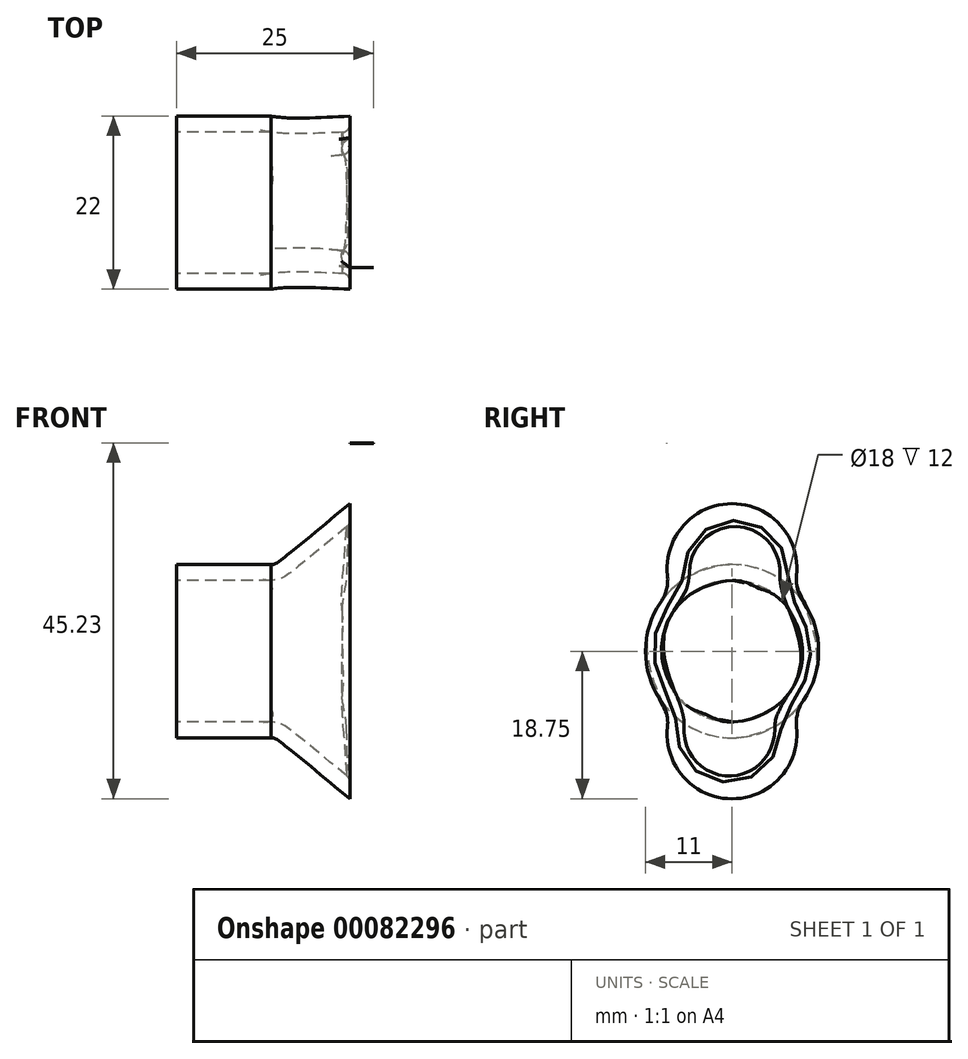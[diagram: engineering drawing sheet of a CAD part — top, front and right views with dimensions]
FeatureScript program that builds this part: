
annotation { "Feature Type Name" : "Feature", "Feature Type Description" : "" }
export const myFeature = defineFeature(function(context is Context, id is Id, definition is map)
    precondition{}
    {
        {
            var Q0;
            Q0=qCreatedBy(makeId("Right.planeOp"),FACE);
            cPlane(context, id + "F0", {"entities" : qUnion([Q0]), "cplaneType" : CPlaneType.OFFSET, "offset" : 10 * mm, "oppositeDirection" : true, "width" : 150 * mm, "height" : 150 * mm});
        }
        {
            var Q0;
            Q0=qCreatedBy(makeId("Right.planeOp"),FACE);
            var sketch = newSketch(context, id + "F1", { "sketchPlane" : qUnion([Q0])});
            skArc(sketch, "E0", {"start": v(-8.2, -9.62) * mm, "mid": v(0, -18.75) * mm, "end": v(8.2, -9.62) * mm});
            skArc(sketch, "E1", {"start": v(8.2, 9.62) * mm, "mid": v(0, 18.75) * mm, "end": v(-8.2, 9.62) * mm});
            skArc(sketch, "E2", {"start": v(9.06, -6.24) * mm, "mid": v(11, 0) * mm, "end": v(9.06, 6.24) * mm});
            skPoint(sketch, "E3.visualSharp", {"position": v(-7.79, -7.77) * mm});
            skArc(sketch, "E3.filletArc", {"start": v(-8.2, -9.62) * mm, "mid": v(-8.33, -7.85) * mm, "end": v(-9.06, -6.24) * mm});
            skPoint(sketch, "E4.visualSharp", {"position": v(7.79, -7.77) * mm});
            skArc(sketch, "E4.filletArc", {"start": v(9.06, -6.24) * mm, "mid": v(8.33, -7.85) * mm, "end": v(8.2, -9.62) * mm});
            skArc(sketch, "E5.trimOffspring", {"start": v(-9.06, 6.24) * mm, "mid": v(-11, 0) * mm, "end": v(-9.06, -6.24) * mm});
            skPoint(sketch, "E6.visualSharp", {"position": v(-7.79, 7.77) * mm});
            skArc(sketch, "E6.filletArc", {"start": v(-9.06, 6.24) * mm, "mid": v(-8.33, 7.85) * mm, "end": v(-8.2, 9.62) * mm});
            skPoint(sketch, "E7.visualSharp", {"position": v(7.79, 7.77) * mm});
            skArc(sketch, "E7.filletArc", {"start": v(8.2, 9.62) * mm, "mid": v(8.33, 7.85) * mm, "end": v(9.06, 6.24) * mm});
            skSolve(sketch);
        }
        {
            var Q0;
            Q0=qCreatedBy(id+"F0.planeOp",FACE);
            var sketch = newSketch(context, id + "F2", { "sketchPlane" : qUnion([Q0])});
            skCircle(sketch, "E8", {"center": v(0, 0) * mm, "radius": 11 * mm});
            skSolve(sketch);
        }
        {
            var Q0;
            Q0=makeQuery(id+"F1.imprint","IMPRINT",FACE,{"disambiguationData":[TD([[makeQuery(id+"F1.imprint","IMPRINT",EDGE,{"derivedFrom":sQuery(id+"F1.wireOp",EDGE,"E0")}),1.0]])]});
            var Q1;
            Q1=makeQuery(id+"F2.imprint","IMPRINT",FACE,{"disambiguationData":[TD([[makeQuery(id+"F2.imprint","IMPRINT",EDGE,{"derivedFrom":sQuery(id+"F2.wireOp",EDGE,"E8")}),1.0]])]});
            loft(context, id + "F3", {"sheetProfilesArray" : [{ "sheetProfileEntities" : qUnion([Q0]) }, { "sheetProfileEntities" : qUnion([Q1]) }]});
        }
        {
            var Q0;
            Q0=makeQuery(id+"F3.opLoft","CAP_FACE",FACE,{"disambiguationData":[OSD([makeQuery(id+"F2.imprint","IMPRINT",FACE,{"disambiguationData":[TD([[makeQuery(id+"F2.imprint","IMPRINT",EDGE,{"derivedFrom":sQuery(id+"F2.wireOp",EDGE,"E8")}),1.0]])]})])],"isStart":true});
            var Q1;
            Q1=makeQuery(id+"F3.opLoft","CAP_FACE",FACE,{"disambiguationData":[OSD([makeQuery(id+"F1.imprint","IMPRINT",FACE,{"disambiguationData":[TD([[makeQuery(id+"F1.imprint","IMPRINT",EDGE,{"derivedFrom":sQuery(id+"F1.wireOp",EDGE,"E0")}),1.0]])]})])],"isStart":true});
            shell(context, id + "F4", {"entities" : qUnion([Q0, Q1]), "thickness" : 2 * mm});
        }
        {
            var Q0;
            Q0=makeQuery(id+"F2.imprint","IMPRINT",FACE,{"disambiguationData":[TD([[makeQuery(id+"F2.imprint","IMPRINT",EDGE,{"derivedFrom":sQuery(id+"F2.wireOp",EDGE,"E8")}),1.0]])]});
            extrude(context, id + "F5", {"entities" : qUnion([Q0]), "operationType" : NewBodyOperationType.ADD, "oppositeDirection" : true, "depth" : 12 * mm, "offsetDistance" : 25 * mm});
        }
        {
            var Q0;
            Q0=makeQuery(id+"F5.opExtrude","CAP_FACE",FACE,{"disambiguationData":[OSD([sQuery(id+"F2.wireOp",EDGE,"E8")])],"isStart":false});
            var sketch = newSketch(context, id + "F6", { "sketchPlane" : qUnion([Q0])});
            skPoint(sketch, "E9", {"position": v(0, 0) * mm});
            skSolve(sketch);
        }
        {
            var Q0;
            Q0=sQuery(id+"F6.wireOp",VERTEX,"E9");
            var Q1;
            Q1=makeQuery(id+"F3.opLoft","SWEPT_BODY",BODY,{"disambiguationData":[OSD([makeQuery(id+"F1.imprint","IMPRINT",FACE,{"disambiguationData":[TD([[makeQuery(id+"F1.imprint","IMPRINT",EDGE,{"derivedFrom":sQuery(id+"F1.wireOp",EDGE,"E0")}),1.0]])]}),makeQuery(id+"F2.imprint","IMPRINT",FACE,{"disambiguationData":[TD([[makeQuery(id+"F2.imprint","IMPRINT",EDGE,{"derivedFrom":sQuery(id+"F2.wireOp",EDGE,"E8")}),1.0]])]})])]});
            hole(context, id + "F7", {"style" : HoleStyle.SIMPLE, "endStyle" : HoleEndStyle.BLIND, "holeDiameter" : 18 * mm, "majorDiameter" : 5 * mm, "holeDepth" : 12 * mm, "isTappedThrough" : true, "tappedDepth" : 12 * mm, "tapClearance" : 3, "startFromSketch" : true, "locations" : qUnion([Q0]), "scope" : qUnion([Q1])});
        }
        {
            var Q0;
            Q0=qCreatedBy(makeId("Right.planeOp"),FACE);
            var sketch = newSketch(context, id + "F8", { "sketchPlane" : qUnion([Q0])});
            skArc(sketch, "E10", {"start": v(8.25, 26.48) * mm, "mid": v(-0.04, 34.73) * mm, "end": v(-8.25, 26.4) * mm});
            skArc(sketch, "E11", {"start": v(-8.25, -25.27) * mm, "mid": v(0, -33.52) * mm, "end": v(8.25, -25.27) * mm});
            skCircle(sketch, "E12", {"center": v(0, 26.48) * mm, "radius": 2.25 * mm});
            skCircle(sketch, "E13", {"center": v(0, -25.27) * mm, "radius": 2.25 * mm});
            skPoint(sketch, "E14.end.orphan", {"position": v(8.25, -25.27) * mm});
            skPoint(sketch, "E14.start.orphan", {"position": v(8.25, 26.48) * mm});
            skPoint(sketch, "E15.end.orphan", {"position": v(-8.25, -25.27) * mm});
            skPoint(sketch, "E15.start.orphan", {"position": v(-8.25, 26.48) * mm});
            skLineSegment(sketch, "E16", {"start": v(8.25, -25.27) * mm, "end": v(8.25, -8.97) * mm});
            skLineSegment(sketch, "E17", {"start": v(-8.25, -8.97) * mm, "end": v(-8.25, -25.27) * mm});
            skLineSegment(sketch, "E18", {"start": v(8.25, 26.48) * mm, "end": v(8.25, 8.97) * mm});
            skLineSegment(sketch, "E19", {"start": v(-8.25, 26.4) * mm, "end": v(-8.25, 26.48) * mm});
            skArc(sketch, "E20", {"start": v(-9.1, 6.17) * mm, "mid": v(-11, 0) * mm, "end": v(-9.1, -6.17) * mm});
            skLineSegment(sketch, "E21", {"start": v(-8.25, 26.4) * mm, "end": v(-8.25, 8.97) * mm});
            skPoint(sketch, "E22.orphan", {"position": v(-8.25, -11.06) * mm});
            skArc(sketch, "E23.trimOffspring", {"start": v(9.1, -6.17) * mm, "mid": v(11, 0) * mm, "end": v(9.1, 6.17) * mm});
            skPoint(sketch, "E24.visualSharp", {"position": v(-8.25, 7.28) * mm});
            skArc(sketch, "E24.filletArc", {"start": v(-9.1, 6.17) * mm, "mid": v(-8.47, 7.5) * mm, "end": v(-8.25, 8.97) * mm});
            skPoint(sketch, "E25.visualSharp", {"position": v(8.25, 7.28) * mm});
            skArc(sketch, "E25.filletArc", {"start": v(8.25, 8.97) * mm, "mid": v(8.47, 7.5) * mm, "end": v(9.1, 6.17) * mm});
            skPoint(sketch, "E26.visualSharp", {"position": v(8.25, -7.28) * mm});
            skArc(sketch, "E26.filletArc", {"start": v(9.1, -6.17) * mm, "mid": v(8.47, -7.5) * mm, "end": v(8.25, -8.97) * mm});
            skPoint(sketch, "E27.visualSharp", {"position": v(-8.25, -7.28) * mm});
            skArc(sketch, "E27.filletArc", {"start": v(-8.25, -8.97) * mm, "mid": v(-8.47, -7.5) * mm, "end": v(-9.1, -6.17) * mm});
            skArc(sketch, "E28", {"start": v(-6.99, 5.67) * mm, "mid": v(-9, -0.1) * mm, "end": v(-6.85, -5.84) * mm});
            skArc(sketch, "E29", {"start": v(5.93, 9.58) * mm, "mid": v(0, 16.5) * mm, "end": v(-5.93, 9.58) * mm});
            skArc(sketch, "E30", {"start": v(-5.7, -9.74) * mm, "mid": v(0, -16.25) * mm, "end": v(5.7, -9.74) * mm});
            skArc(sketch, "E31.trimOffspring", {"start": v(6.85, -5.84) * mm, "mid": v(9, -0.1) * mm, "end": v(6.99, 5.67) * mm});
            skPoint(sketch, "E32.visualSharp", {"position": v(-4.93, -7.53) * mm});
            skArc(sketch, "E32.filletArc", {"start": v(-5.7, -9.74) * mm, "mid": v(-5.86, -7.67) * mm, "end": v(-6.85, -5.84) * mm});
            skPoint(sketch, "E33.visualSharp", {"position": v(4.93, -7.53) * mm});
            skArc(sketch, "E33.filletArc", {"start": v(6.85, -5.84) * mm, "mid": v(5.86, -7.67) * mm, "end": v(5.7, -9.74) * mm});
            skPoint(sketch, "E34.visualSharp", {"position": v(5.13, 7.4) * mm});
            skArc(sketch, "E34.filletArc", {"start": v(5.93, 9.58) * mm, "mid": v(6.04, 7.52) * mm, "end": v(6.99, 5.67) * mm});
            skPoint(sketch, "E35.visualSharp", {"position": v(-5.13, 7.4) * mm});
            skArc(sketch, "E35.filletArc", {"start": v(-6.99, 5.67) * mm, "mid": v(-6.04, 7.52) * mm, "end": v(-5.93, 9.58) * mm});
            skSolve(sketch);
        }
        {
            var Q0;
            Q0=makeQuery(id+"F8.imprint","IMPRINT",FACE,{"disambiguationData":[TD([[makeQuery(id+"F8.imprint","IMPRINT",EDGE,{"derivedFrom":sQuery(id+"F8.wireOp",EDGE,"E10")}),1.0]])]});
            extrude(context, id + "F9", {"entities" : qUnion([Q0]), "operationType" : NewBodyOperationType.ADD, "depth" : 3 * mm, "offsetDistance" : 25 * mm});
        }
        {
            var Q0;
            {var subQ1=sQuery(id+"F8.wireOp",EDGE,"E29");var subQ2=sQuery(id+"F1.wireOp",EDGE,"E7.filletArc");var subQ3=sQuery(id+"F1.wireOp",EDGE,"E6.filletArc");var subQ4=sQuery(id+"F1.wireOp",EDGE,"E5.trimOffspring");var subQ5=sQuery(id+"F1.wireOp",EDGE,"E4.filletArc");var subQ6=sQuery(id+"F1.wireOp",EDGE,"E3.filletArc");var subQ7=sQuery(id+"F1.wireOp",EDGE,"E2");var subQ8=sQuery(id+"F1.wireOp",EDGE,"E1");var subQ9=sQuery(id+"F1.wireOp",EDGE,"E0");var subQ10=makeQuery(id+"F4.opShell","OFFSET_FACE",FACE,{"disambiguationData":[OSD([subQ9,subQ8,subQ7,subQ6,subQ5,subQ4,subQ3,subQ2,sQuery(id+"F2.wireOp",EDGE,"E8")])]});var subQ11=makeQuery(id+"F3.opLoft","CAP_FACE",FACE,{"disambiguationData":[OSD([makeQuery(id+"F1.imprint","IMPRINT",FACE,{"disambiguationData":[TD([[makeQuery(id+"F1.imprint","IMPRINT",EDGE,{"derivedFrom":subQ9}),1.0]])]})])],"isStart":true});Q0=makeQuery(id+"F9.boolean.opBoolean","SPLIT",EDGE,{"disambiguationData":[topologyDisambiguationEdgeConnected([subQ11,subQ10]),TD([makeQuery(id+"F9.opExtrude","SWEPT_FACE",FACE,{"disambiguationData":[OSD([subQ1])]})])],"derivedFrom":makeQuery(id+"F4.opShell","OFFSET_EDGE",EDGE,{"disambiguationData":[OSD([subQ9,subQ8,subQ7,subQ6,subQ5,subQ4,subQ3,subQ2])]})});}
            fillet(context, id + "F10", {"entities" : qUnion([Q0]), "tangentPropagation" : true, "radius" : 1 * mm, "defaultsChanged" : true, "vertexSettings" : [], "allowEdgeOverflow" : false});
        }
    });
